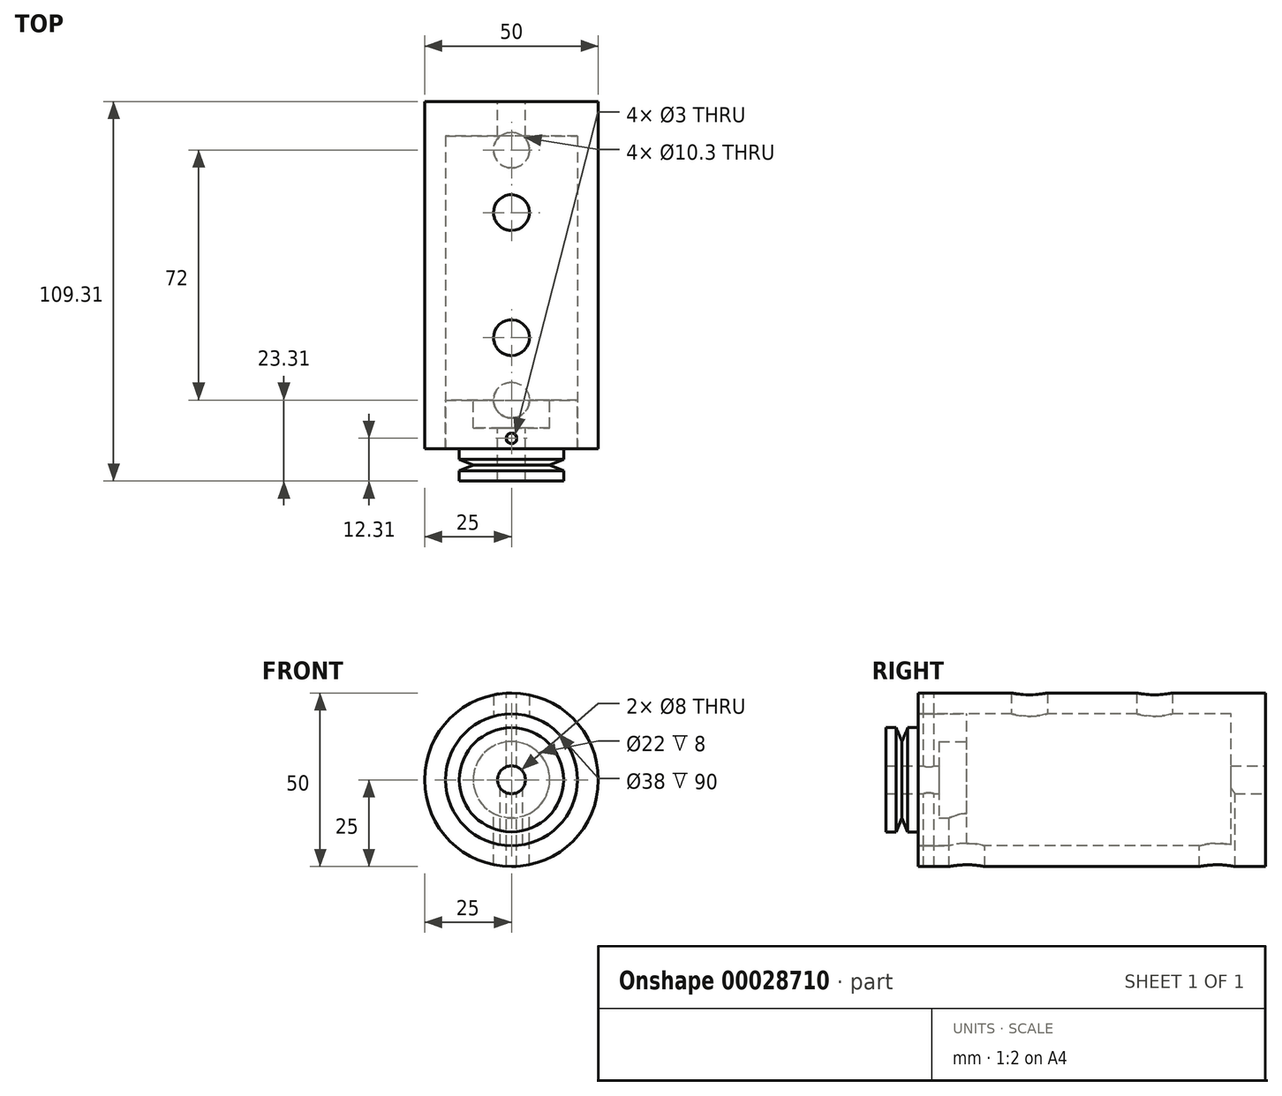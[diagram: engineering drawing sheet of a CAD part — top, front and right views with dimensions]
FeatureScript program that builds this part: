
annotation { "Feature Type Name" : "Feature", "Feature Type Description" : "" }
export const myFeature = defineFeature(function(context is Context, id is Id, definition is map)
    precondition{}
    {
        {
            var Q0;
            Q0=qCreatedBy(makeId("Front.planeOp"),FACE);
            var sketch = newSketch(context, id + "F0", { "sketchPlane" : qUnion([Q0])});
            skCircle(sketch, "E0", {"center": v(0, 0) * mm, "radius": 25 * mm});
            skCircle(sketch, "E1", {"center": v(0, 0) * mm, "radius": 19 * mm, "construction": true});
            skCircle(sketch, "E2", {"center": v(0, 0) * mm, "radius": 4 * mm});
            skSolve(sketch);
        }
        {
            var Q0;
            Q0 = qSketchRegion(id + "F0", true);
            extrude(context, id + "F1", {"entities" : qUnion([Q0]), "endBound" : BoundingType.SYMMETRIC, "depth" : 100 * mm, "offsetDistance" : 25 * mm});
        }
        {
            var Q0;
            Q0=qCreatedBy(makeId("Front.planeOp"),FACE);
            var sketch = newSketch(context, id + "F2", { "sketchPlane" : qUnion([Q0])});
            skCircle(sketch, "E3.0", {"center": v(0, 0) * mm, "radius": 19 * mm});
            skSolve(sketch);
        }
        {
            var Q0;
            Q0 = qSketchRegion(id + "F2", true);
            var Q1;
            Q1=makeQuery(id+"F1.opExtrude","CAP_FACE",FACE,{"disambiguationData":[OSD([sQuery(id+"F0.wireOp",EDGE,"E0")])],"isStart":true});
            extrude(context, id + "F3", {"entities" : qUnion([Q0]), "operationType" : NewBodyOperationType.REMOVE, "endBound" : BoundingType.UP_TO_SURFACE, "oppositeDirection" : true, "depth" : 25 * mm, "endBoundEntityFace" : qUnion([Q1]), "hasOffset" : true, "offsetDistance" : 10 * mm, "hasSecondDirection" : true, "secondDirectionBound" : SecondDirectionBoundingType.THROUGH_ALL, "secondDirectionOppositeDirection" : false, "secondDirectionDepth" : 25 * mm});
        }
        {
            var Q0;
            Q0=qCreatedBy(makeId("Top.planeOp"),FACE);
            var sketch = newSketch(context, id + "F4", { "sketchPlane" : qUnion([Q0])});
            skLineSegment(sketch, "E4", {"start": v(0, 0) * mm, "end": v(0, -46.54) * mm, "construction": true});
            skLineSegment(sketch, "E5", {"start": v(4, -44) * mm, "end": v(11, -44) * mm});
            skLineSegment(sketch, "E6", {"start": v(11, -44) * mm, "end": v(11, -36) * mm});
            skLineSegment(sketch, "E7", {"start": v(11, -36) * mm, "end": v(19, -36) * mm});
            skLineSegment(sketch, "E8", {"start": v(19, -36) * mm, "end": v(19, -50) * mm});
            skLineSegment(sketch, "E9", {"start": v(19, -50) * mm, "end": v(15, -50) * mm});
            skLineSegment(sketch, "E10", {"start": v(15, -50) * mm, "end": v(15, -53) * mm});
            skLineSegment(sketch, "E11", {"start": v(15, -53) * mm, "end": v(11, -54.66) * mm});
            skLineSegment(sketch, "E12", {"start": v(11, -54.66) * mm, "end": v(15, -56.31) * mm});
            skLineSegment(sketch, "E13", {"start": v(15, -56.31) * mm, "end": v(15, -59.31) * mm});
            skLineSegment(sketch, "E14", {"start": v(15, -59.31) * mm, "end": v(4, -59.31) * mm});
            skLineSegment(sketch, "E15", {"start": v(4, -59.31) * mm, "end": v(4, -44) * mm});
            skLineSegment(sketch, "E16", {"start": v(11, -54.66) * mm, "end": v(15, -54.66) * mm, "construction": true});
            skLineSegment(sketch, "E17", {"start": v(15, -53) * mm, "end": v(15, -56.31) * mm, "construction": true});
            skSolve(sketch);
        }
        {
            var Q0;
            Q0 = qSketchRegion(id + "F4", true);
            var Q1;
            Q1=sQuery(id+"F4.wireOp",EDGE,"E4");
            revolve(context, id + "F5", {"surfaceOperationType" : NewSurfaceOperationType.NEW, "entities" : qUnion([Q0]), "axis" : qUnion([Q1]), "revolveType" : RevolveType.FULL});
        }
        {
            var Q0;
            Q0=qCreatedBy(makeId("Top.planeOp"),FACE);
            var sketch = newSketch(context, id + "F6", { "sketchPlane" : qUnion([Q0])});
            skCircle(sketch, "E18", {"center": v(0, -47) * mm, "radius": 1.5 * mm});
            skSolve(sketch);
        }
        {
            var Q0;
            Q0 = qSketchRegion(id + "F6", true);
            extrude(context, id + "F7", {"entities" : qUnion([Q0]), "operationType" : NewBodyOperationType.REMOVE, "endBound" : BoundingType.THROUGH_ALL, "oppositeDirection" : true, "depth" : 25 * mm, "offsetDistance" : 25 * mm, "hasSecondDirection" : true, "secondDirectionBound" : SecondDirectionBoundingType.THROUGH_ALL, "secondDirectionOppositeDirection" : false, "secondDirectionDepth" : 25 * mm});
        }
        {
            var Q0;
            Q0=qCreatedBy(makeId("Top.planeOp"),FACE);
            var sketch = newSketch(context, id + "F8", { "sketchPlane" : qUnion([Q0])});
            skPoint(sketch, "E19", {"position": v(0, 36) * mm});
            skPoint(sketch, "E20", {"position": v(0, 18) * mm});
            skPoint(sketch, "E21", {"position": v(0, -18) * mm});
            skPoint(sketch, "E22", {"position": v(0, -36) * mm});
            skLineSegment(sketch, "E23", {"start": v(0, 36) * mm, "end": v(0, 50) * mm, "construction": true});
            skLineSegment(sketch, "E24", {"start": v(0, 18) * mm, "end": v(0, 0) * mm, "construction": true});
            skLineSegment(sketch, "E25", {"start": v(0, 0) * mm, "end": v(0, -18) * mm, "construction": true});
            skLineSegment(sketch, "E26", {"start": v(0, 18) * mm, "end": v(0, 36) * mm, "construction": true});
            skLineSegment(sketch, "E27", {"start": v(0, -18) * mm, "end": v(0, -36) * mm, "construction": true});
            skLineSegment(sketch, "E28", {"start": v(0, -36) * mm, "end": v(0, -50) * mm, "construction": true});
            skSolve(sketch);
        }
        {
            var Q0;
            Q0=sQuery(id+"F8.wireOp",VERTEX,"E19");
            var Q1;
            Q1=sQuery(id+"F8.wireOp",VERTEX,"E22");
            var Q2;
            Q2=makeQuery(id+"F1.opExtrude","SWEPT_BODY",BODY,{"disambiguationData":[OSD([sQuery(id+"F0.wireOp",EDGE,"E0"),sQuery(id+"F0.wireOp",EDGE,"E2")])]});
            var Q3;
            Q3=makeQuery(id+"F5.opRevolve","SWEPT_BODY",BODY,{"disambiguationData":[OSD([sQuery(id+"F4.wireOp",EDGE,"E5"),sQuery(id+"F4.wireOp",EDGE,"E6"),sQuery(id+"F4.wireOp",EDGE,"E7"),sQuery(id+"F4.wireOp",EDGE,"E8"),sQuery(id+"F4.wireOp",EDGE,"E9"),sQuery(id+"F4.wireOp",EDGE,"E10"),sQuery(id+"F4.wireOp",EDGE,"E11"),sQuery(id+"F4.wireOp",EDGE,"E12"),sQuery(id+"F4.wireOp",EDGE,"E13"),sQuery(id+"F4.wireOp",EDGE,"E14"),sQuery(id+"F4.wireOp",EDGE,"E15")])]});
            hole(context, id + "F9", {"style" : HoleStyle.SIMPLE, "endStyle" : HoleEndStyle.BLIND, "standardTappedOrClearance" : lookupTablePath({ "standard" : "ISO", "engagement" : "75%", "pitch" : "1.75 mm", "size" : "M12", "type" : "Tapped" }), "standardBlindInLast" : lookupTablePath({ "standard" : "ISO", "fit" : "Normal", "engagement" : "75%", "pitch" : "1.75 mm", "size" : "M12", "type" : "Clearance & tapped" }), "holeDiameter" : 10.3 * mm, "majorDiameter" : 12 * mm, "showTappedDepth" : true, "holeDepth" : 17.25 * mm, "isTappedThrough" : true, "tappedDepth" : 12 * mm, "tapClearance" : 3, "locations" : qUnion([Q0, Q1]), "scope" : qUnion([Q2, Q3])});
        }
        {
            var Q0;
            Q0=sQuery(id+"F8.wireOp",VERTEX,"E20");
            var Q1;
            Q1=sQuery(id+"F8.wireOp",VERTEX,"E21");
            var Q2;
            Q2=makeQuery(id+"F1.opExtrude","SWEPT_BODY",BODY,{"disambiguationData":[OSD([sQuery(id+"F0.wireOp",EDGE,"E0"),sQuery(id+"F0.wireOp",EDGE,"E2")])]});
            hole(context, id + "F10", {"style" : HoleStyle.SIMPLE, "endStyle" : HoleEndStyle.BLIND, "oppositeDirection" : true, "standardTappedOrClearance" : lookupTablePath({ "standard" : "ISO", "engagement" : "75%", "pitch" : "1.75 mm", "size" : "M12", "type" : "Tapped" }), "standardBlindInLast" : lookupTablePath({ "fit" : "Normal", "standard" : "ISO", "engagement" : "75%", "pitch" : "1.75 mm", "size" : "M12", "type" : "Clearance & tapped" }), "holeDiameter" : 10.3 * mm, "majorDiameter" : 12 * mm, "showTappedDepth" : true, "holeDepth" : 17.25 * mm, "isTappedThrough" : true, "tappedDepth" : 12 * mm, "tapClearance" : 3, "locations" : qUnion([Q0, Q1]), "scope" : qUnion([Q2])});
        }
    });
